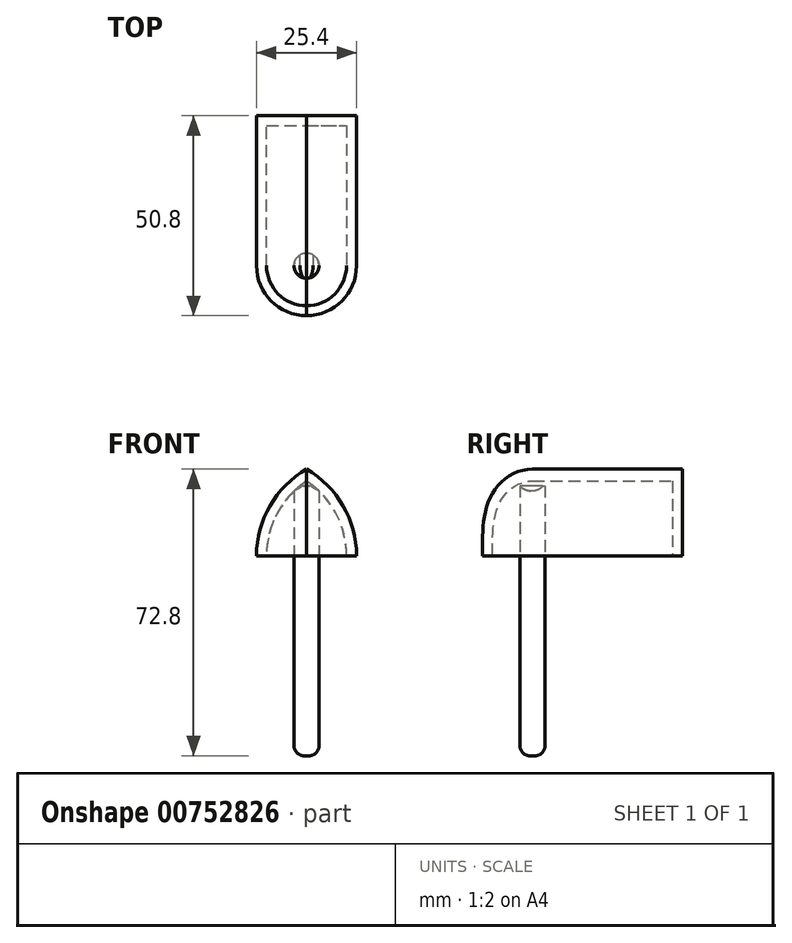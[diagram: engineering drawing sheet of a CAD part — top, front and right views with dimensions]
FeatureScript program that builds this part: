
annotation { "Feature Type Name" : "Feature", "Feature Type Description" : "" }
export const myFeature = defineFeature(function(context is Context, id is Id, definition is map)
    precondition{}
    {
        {
            var Q0;
            Q0=qCreatedBy(makeId("Top.planeOp"),FACE);
            var sketch = newSketch(context, id + "F0", { "sketchPlane" : qUnion([Q0])});
            skLineSegment(sketch, "E0.bottom", {"start": v(0, 0) * mm, "end": v(25.4, 0) * mm});
            skLineSegment(sketch, "E0.top", {"start": v(0, 50.8) * mm, "end": v(25.4, 50.8) * mm});
            skLineSegment(sketch, "E0.left", {"start": v(0, 0) * mm, "end": v(0, 50.8) * mm});
            skLineSegment(sketch, "E0.right", {"start": v(25.4, 0) * mm, "end": v(25.4, 50.8) * mm});
            skSolve(sketch);
        }
        {
            var Q0;
            Q0=makeQuery(id+"F0.imprint","IMPRINT",FACE,{"disambiguationData":[TD([[makeQuery(id+"F0.imprint","IMPRINT",EDGE,{"derivedFrom":sQuery(id+"F0.wireOp",EDGE,"E0.bottom")}),1.0]])]});
            extrude(context, id + "F1", {"entities" : qUnion([Q0]), "depth" : 25.4 * mm, "offsetDistance" : 25.4 * mm});
        }
        {
            var Q0;
            Q0=makeQuery(id+"F1.opExtrude","CAP_EDGE",EDGE,{"disambiguationData":[OSD([sQuery(id+"F0.wireOp",EDGE,"E0.right")])],"isStart":false});
            var Q1;
            Q1=makeQuery(id+"F1.opExtrude","CAP_EDGE",EDGE,{"disambiguationData":[OSD([sQuery(id+"F0.wireOp",EDGE,"E0.left")])],"isStart":false});
            fillet(context, id + "F2", {"entities" : qUnion([Q0, Q1]), "radius" : 25.4 * mm, "tangentPropagation" : true, "allowEdgeOverflow" : false});
        }
        {
            var Q0;
            Q0=makeQuery(id+"F2.opFillet","BLEND_EDGE",EDGE,{"blendedFrom":[makeQuery(id+"F1.opExtrude","CAP_EDGE",EDGE,{"disambiguationData":[OSD([sQuery(id+"F0.wireOp",EDGE,"E0.right")])],"isStart":false}),makeQuery(id+"F1.opExtrude","SWEPT_FACE",FACE,{"disambiguationData":[OSD([sQuery(id+"F0.wireOp",EDGE,"E0.bottom")])]})],"blendedInto":[makeQuery(id+"F1.opExtrude","SWEPT_FACE",FACE,{"disambiguationData":[OSD([sQuery(id+"F0.wireOp",EDGE,"E0.bottom")])]})]});
            var Q1;
            Q1=makeQuery(id+"F2.opFillet","BLEND_EDGE",EDGE,{"blendedFrom":[makeQuery(id+"F1.opExtrude","CAP_EDGE",EDGE,{"disambiguationData":[OSD([sQuery(id+"F0.wireOp",EDGE,"E0.left")])],"isStart":false}),makeQuery(id+"F1.opExtrude","SWEPT_FACE",FACE,{"disambiguationData":[OSD([sQuery(id+"F0.wireOp",EDGE,"E0.bottom")])]})],"blendedInto":[makeQuery(id+"F1.opExtrude","SWEPT_FACE",FACE,{"disambiguationData":[OSD([sQuery(id+"F0.wireOp",EDGE,"E0.bottom")])]})]});
            fillet(context, id + "F3", {"entities" : qUnion([Q0, Q1]), "radius" : 12.7 * mm, "tangentPropagation" : true, "allowEdgeOverflow" : false});
        }
        {
            var Q0;
            Q0=makeQuery(id+"F1.opExtrude","CAP_FACE",FACE,{"disambiguationData":[OSD([sQuery(id+"F0.wireOp",EDGE,"E0.bottom"),sQuery(id+"F0.wireOp",EDGE,"E0.top"),sQuery(id+"F0.wireOp",EDGE,"E0.left"),sQuery(id+"F0.wireOp",EDGE,"E0.right")])],"isStart":true});
            shell(context, id + "F4", {"entities" : qUnion([Q0]), "thickness" : 2.54 * mm});
        }
        {
            var Q0;
            Q0=qCreatedBy(makeId("Top.planeOp"),FACE);
            var sketch = newSketch(context, id + "F5", { "sketchPlane" : qUnion([Q0])});
            skCircle(sketch, "E1", {"center": v(12.7, 12.7) * mm, "radius": 3.18 * mm});
            skSolve(sketch);
        }
        {
            var Q0;
            Q0=makeQuery(id+"F5.imprint","IMPRINT",FACE,{"disambiguationData":[TD([[makeQuery(id+"F5.imprint","IMPRINT",EDGE,{"derivedFrom":sQuery(id+"F5.wireOp",EDGE,"E1")}),1.0]])]});
            extrude(context, id + "F6", {"entities" : qUnion([Q0]), "operationType" : NewBodyOperationType.ADD, "depth" : 17.78 * mm, "offsetDistance" : 25.4 * mm});
        }
        {
            var Q0;
            Q0=makeQuery(id+"F6.opExtrude","CAP_FACE",FACE,{"disambiguationData":[OSD([sQuery(id+"F5.wireOp",EDGE,"E1")])],"isStart":true});
            var sketch = newSketch(context, id + "F7", { "sketchPlane" : qUnion([Q0])});
            skCircle(sketch, "E2", {"center": v(12.7, -12.7) * mm, "radius": 3.18 * mm});
            skSolve(sketch);
        }
        {
            var Q0;
            Q0=makeQuery(id+"F7.imprint","IMPRINT",FACE,{"disambiguationData":[TD([[makeQuery(id+"F7.imprint","IMPRINT",EDGE,{"derivedFrom":sQuery(id+"F7.wireOp",EDGE,"E2")}),-1.0]])]});
            extrude(context, id + "F8", {"entities" : qUnion([Q0]), "operationType" : NewBodyOperationType.ADD, "depth" : 50.8 * mm, "offsetDistance" : 25.4 * mm});
        }
        {
            var Q0;
            Q0=makeQuery(id+"F8.opExtrude","CAP_EDGE",EDGE,{"disambiguationData":[OSD([sQuery(id+"F7.wireOp",EDGE,"E2")])],"isStart":false});
            fillet(context, id + "F9", {"entities" : qUnion([Q0]), "radius" : 2.54 * mm, "tangentPropagation" : true, "allowEdgeOverflow" : false});
        }
    });
